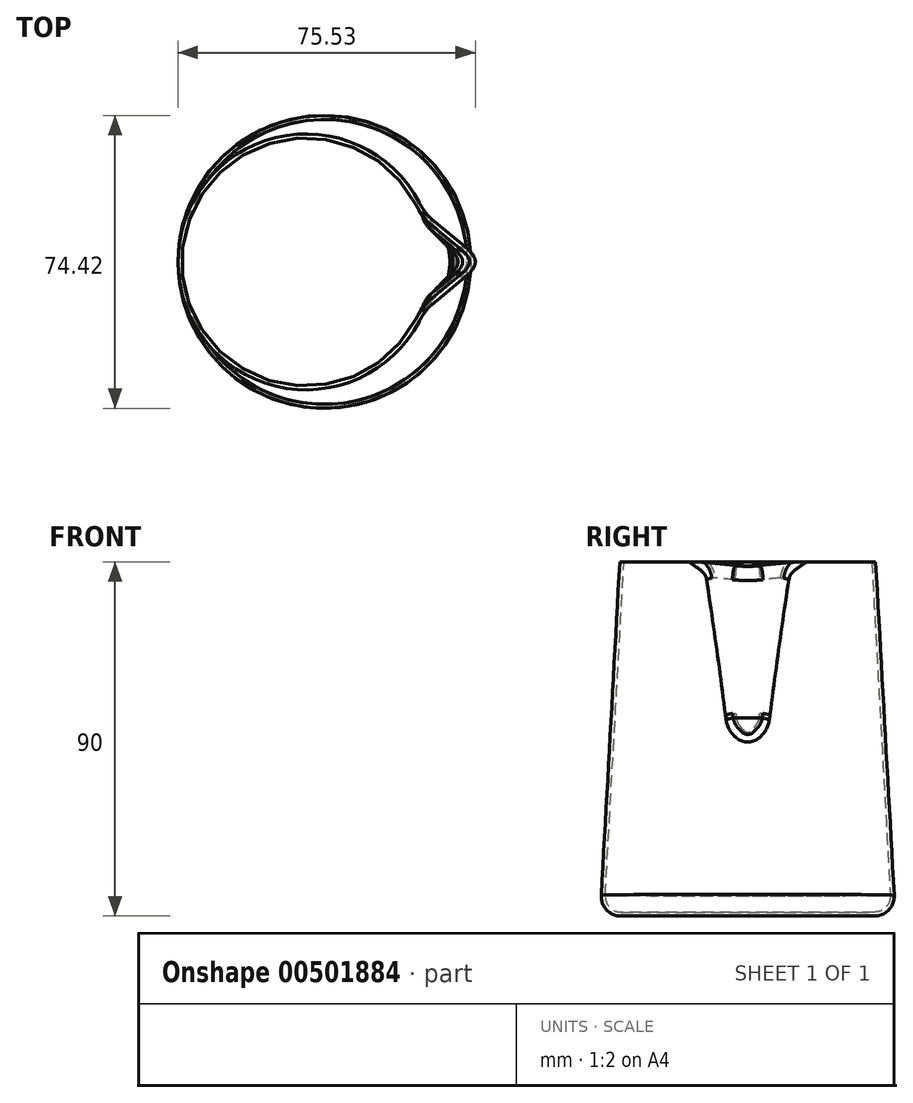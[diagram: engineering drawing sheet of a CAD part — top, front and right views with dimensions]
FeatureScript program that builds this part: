
annotation { "Feature Type Name" : "Feature", "Feature Type Description" : "" }
export const myFeature = defineFeature(function(context is Context, id is Id, definition is map)
    precondition{}
    {
        {
            var Q0;
            Q0=qCreatedBy(makeId("Top.planeOp"),FACE);
            var sketch = newSketch(context, id + "F0", { "sketchPlane" : qUnion([Q0])});
            skCircle(sketch, "E0", {"center": v(0, 0) * mm, "radius": 37.5 * mm});
            skSolve(sketch);
        }
        {
            var Q0;
            Q0=qCreatedBy(makeId("Top.planeOp"),FACE);
            cPlane(context, id + "F1", {"entities" : qUnion([Q0]), "cplaneType" : CPlaneType.OFFSET, "offset" : 90 * mm, "width" : 150 * mm, "height" : 150 * mm});
        }
        {
            var Q0;
            Q0=qCreatedBy(id+"F1.planeOp",FACE);
            var sketch = newSketch(context, id + "F2", { "sketchPlane" : qUnion([Q0])});
            skCircle(sketch, "E1", {"center": v(-5, 0) * mm, "radius": 32.5 * mm});
            skLineSegment(sketch, "E2", {"start": v(-111.32, 0) * mm, "end": v(0, 0) * mm, "construction": true});
            skSolve(sketch);
        }
        {
            var Q0;
            Q0=qCreatedBy(id+"F1.planeOp",FACE);
            var sketch = newSketch(context, id + "F3", { "sketchPlane" : qUnion([Q0])});
            skLineSegment(sketch, "E3", {"start": v(25, 44.02) * mm, "end": v(25, -44.23) * mm, "construction": true});
            skSolve(sketch);
        }
        {
            var Q0;
            Q0=qCreatedBy(id+"F1.planeOp",FACE);
            var Q1;
            Q1=sQuery(id+"F3.wireOp",EDGE,"E3");
            cPlane(context, id + "F4", {"entities" : qUnion([Q0, Q1]), "cplaneType" : CPlaneType.LINE_ANGLE, "offset" : 25 * mm, "angle" : 5 * degree, "oppositeDirection" : true, "width" : 150 * mm, "height" : 150 * mm});
        }
        {
            var Q0;
            Q0=qCreatedBy(id+"F4.planeOp",FACE);
            var sketch = newSketch(context, id + "F5", { "sketchPlane" : qUnion([Q0])});
            skLineSegment(sketch, "E4", {"start": v(17.06, -12.5) * mm, "end": v(32.06, 0) * mm});
            skLineSegment(sketch, "E5", {"start": v(0, 0) * mm, "end": v(86.07, 0) * mm, "construction": true});
            skPoint(sketch, "E6", {"position": v(43.04, 0) * mm});
            skLineSegment(sketch, "E7.MirrorCS", {"start": v(17.06, 12.5) * mm, "end": v(32.06, 0) * mm});
            skLineSegment(sketch, "E8", {"start": v(17.06, -12.5) * mm, "end": v(17.06, 12.5) * mm});
            skSolve(sketch);
        }
        {
            var Q0;
            Q0=makeQuery(id+"F0.imprint","IMPRINT",FACE,{"disambiguationData":[TD([[makeQuery(id+"F0.imprint","IMPRINT",EDGE,{"derivedFrom":sQuery(id+"F0.wireOp",EDGE,"E0")}),1.0]])]});
            var Q1;
            Q1=makeQuery(id+"F2.imprint","IMPRINT",FACE,{"disambiguationData":[TD([[makeQuery(id+"F2.imprint","IMPRINT",EDGE,{"derivedFrom":sQuery(id+"F2.wireOp",EDGE,"E1")}),1.0]])]});
            loft(context, id + "F6", {"sheetProfilesArray" : [{ "sheetProfileEntities" : qUnion([Q0]) }, { "sheetProfileEntities" : qUnion([Q1]) }]});
        }
        {
            var Q0;
            Q0=qCreatedBy(makeId("Front.planeOp"),FACE);
            var sketch = newSketch(context, id + "F7", { "sketchPlane" : qUnion([Q0])});
            skFitSpline(sketch, "E9", {"points": [v(-37.5, 90) * mm, v(-37.5, 0) * mm], "construction": true});
            skLineSegment(sketch, "E10", {"start": v(37.5, 0) * mm, "end": v(27.5, 90) * mm, "construction": true});
            skArc(sketch, "E11", {"start": v(38.1, 84.98) * mm, "mid": v(38.62, 87.04) * mm, "end": v(39.94, 88.7) * mm});
            skLineSegment(sketch, "E12", {"start": v(36.93, 49.98) * mm, "end": v(38.1, 84.98) * mm});
            skArc(sketch, "E13", {"start": v(32.48, 45.18) * mm, "mid": v(35.6, 46.75) * mm, "end": v(36.93, 49.98) * mm});
            skSolve(sketch);
        }
        {
            var Q0;
            Q0=makeQuery(id+"F5.imprint","IMPRINT",FACE,{"disambiguationData":[TD([[makeQuery(id+"F5.imprint","IMPRINT",EDGE,{"derivedFrom":sQuery(id+"F5.wireOp",EDGE,"E4")}),1.0]])]});
            var Q1;
            Q1=sQuery(id+"F7.wireOp",EDGE,"E12");
            var Q2;
            Q2=sQuery(id+"F7.wireOp",EDGE,"E13");
            var Q3;
            Q3=sQuery(id+"F7.wireOp",EDGE,"E11");
            sweep(context, id + "F8", {"operationType" : NewBodyOperationType.ADD, "profiles" : qUnion([Q0]), "path" : qUnion([Q1, Q2, Q3]), "keepProfileOrientation" : true});
        }
        {
            var Q0;
            Q0=qCreatedBy(id+"F4.planeOp",FACE);
            var sketch = newSketch(context, id + "F9", { "sketchPlane" : qUnion([Q0])});
            skLineSegment(sketch, "E14", {"start": v(17.06, -12.5) * mm, "end": v(32.06, 0) * mm});
            skLineSegment(sketch, "E15", {"start": v(32.06, 0) * mm, "end": v(17.06, 12.5) * mm});
            skLineSegment(sketch, "E16", {"start": v(17.06, 12.5) * mm, "end": v(17.06, -12.5) * mm});
            skSolve(sketch);
        }
        {
            var Q0;
            Q0 = qSketchRegion(id + "F9", true);
            extrude(context, id + "F10", {"entities" : qUnion([Q0]), "operationType" : NewBodyOperationType.REMOVE, "oppositeDirection" : true, "depth" : 25 * mm});
        }
        {
            var Q0;
            Q0=makeQuery(id+"F8.opSweep","SWEPT_EDGE",EDGE,{"disambiguationData":[OSD([sQuery(id+"F5.wireOp",EDGE,"E4"),sQuery(id+"F5.wireOp",EDGE,"E7.MirrorCS"),sQuery(id+"F7.wireOp",EDGE,"E12")])]});
            fillet(context, id + "F11", {"entities" : qUnion([Q0]), "radius" : 5 * mm, "tangentPropagation" : true, "rho" : 0.5, "crossSection" : FilletCrossSection.CONIC, "allowEdgeOverflow" : false});
        }
        {
            var Q0;
            Q0=makeQuery(id+"F8.boolean.opBoolean","INTERSECT",EDGE,{"derivedFrom":[makeQuery(id+"F6.opLoft","SWEPT_FACE",FACE,{"disambiguationData":[OSD([sQuery(id+"F0.wireOp",EDGE,"E0"),sQuery(id+"F2.wireOp",EDGE,"E1")])]}),makeQuery(id+"F8.opSweep","SWEPT_FACE",FACE,{"disambiguationData":[OSD([sQuery(id+"F5.wireOp",EDGE,"E7.MirrorCS"),sQuery(id+"F7.wireOp",EDGE,"E12")])]})]});
            var Q1;
            Q1=makeQuery(id+"F8.boolean.opBoolean","INTERSECT",EDGE,{"derivedFrom":[makeQuery(id+"F6.opLoft","SWEPT_FACE",FACE,{"disambiguationData":[OSD([sQuery(id+"F0.wireOp",EDGE,"E0"),sQuery(id+"F2.wireOp",EDGE,"E1")])]}),makeQuery(id+"F8.opSweep","SWEPT_FACE",FACE,{"disambiguationData":[OSD([sQuery(id+"F5.wireOp",EDGE,"E7.MirrorCS"),sQuery(id+"F7.wireOp",EDGE,"E11")])]})]});
            var Q2;
            Q2=makeQuery(id+"F8.boolean.opBoolean","INTERSECT",EDGE,{"derivedFrom":[makeQuery(id+"F6.opLoft","SWEPT_FACE",FACE,{"disambiguationData":[OSD([sQuery(id+"F0.wireOp",EDGE,"E0"),sQuery(id+"F2.wireOp",EDGE,"E1")])]}),makeQuery(id+"F8.opSweep","SWEPT_FACE",FACE,{"disambiguationData":[OSD([sQuery(id+"F5.wireOp",EDGE,"E7.MirrorCS"),sQuery(id+"F7.wireOp",EDGE,"E13")])]})]});
            var Q3;
            {var subQ0=sQuery(id+"F5.wireOp",EDGE,"E7.MirrorCS");var subQ1=sQuery(id+"F5.wireOp",EDGE,"E4");var subQ2=sQuery(id+"F2.wireOp",EDGE,"E1");var subQ3=sQuery(id+"F7.wireOp",EDGE,"E11");var subQ4=sQuery(id+"F0.wireOp",EDGE,"E0");var subQ5=sQuery(id+"F7.wireOp",EDGE,"E13");var subQ6=makeQuery(id+"F6.opLoft","SWEPT_FACE",FACE,{"disambiguationData":[OSD([subQ4,subQ2])]});var subQ7=sQuery(id+"F7.wireOp",EDGE,"E12");Q3=makeQuery(id+"F11.opFillet","BLEND_EDGE",EDGE,{"blendedFrom":[makeQuery(id+"F8.opSweep","SWEPT_EDGE",EDGE,{"disambiguationData":[OSD([subQ1,subQ0,subQ5])]}),makeQuery(id+"F8.boolean.opBoolean","SPLIT",FACE,{"disambiguationData":[TD([subQ6,makeQuery(id+"F6.opLoft","CAP_FACE",FACE,{"disambiguationData":[OSD([makeQuery(id+"F0.imprint","IMPRINT",FACE,{"disambiguationData":[TD([[makeQuery(id+"F0.imprint","IMPRINT",EDGE,{"derivedFrom":subQ4}),1.0]])]})])],"isStart":true}),makeQuery(id+"F6.opLoft","CAP_FACE",FACE,{"disambiguationData":[OSD([makeQuery(id+"F2.imprint","IMPRINT",FACE,{"disambiguationData":[TD([[makeQuery(id+"F2.imprint","IMPRINT",EDGE,{"derivedFrom":subQ2}),1.0]])]})])],"isStart":true}),makeQuery(id+"F8.opSweep","CAP_FACE",FACE,{"disambiguationData":[OSD([subQ1,subQ0,sQuery(id+"F5.wireOp",EDGE,"E8"),sQuery(id+"F7.wireOp",VERTEX,"E11.end")])],"isStart":true}),makeQuery(id+"F8.opSweep","SWEPT_FACE",FACE,{"disambiguationData":[OSD([subQ1,subQ3])]}),makeQuery(id+"F8.opSweep","SWEPT_FACE",FACE,{"disambiguationData":[OSD([subQ1,subQ7])]}),makeQuery(id+"F8.opSweep","SWEPT_FACE",FACE,{"disambiguationData":[OSD([subQ1,subQ5])]}),makeQuery(id+"F8.opSweep","SWEPT_FACE",FACE,{"disambiguationData":[OSD([subQ0,subQ3])]}),makeQuery(id+"F8.opSweep","SWEPT_FACE",FACE,{"disambiguationData":[OSD([subQ0,subQ7])]}),makeQuery(id+"F8.opSweep","SWEPT_FACE",FACE,{"disambiguationData":[OSD([subQ0,subQ5])]})])],"derivedFrom":subQ6})],"blendedInto":[makeQuery(id+"F8.boolean.opBoolean","SPLIT",FACE,{"disambiguationData":[TD([subQ6,makeQuery(id+"F6.opLoft","CAP_FACE",FACE,{"disambiguationData":[OSD([makeQuery(id+"F0.imprint","IMPRINT",FACE,{"disambiguationData":[TD([[makeQuery(id+"F0.imprint","IMPRINT",EDGE,{"derivedFrom":subQ4}),1.0]])]})])],"isStart":true}),makeQuery(id+"F6.opLoft","CAP_FACE",FACE,{"disambiguationData":[OSD([makeQuery(id+"F2.imprint","IMPRINT",FACE,{"disambiguationData":[TD([[makeQuery(id+"F2.imprint","IMPRINT",EDGE,{"derivedFrom":subQ2}),1.0]])]})])],"isStart":true}),makeQuery(id+"F8.opSweep","CAP_FACE",FACE,{"disambiguationData":[OSD([subQ1,subQ0,sQuery(id+"F5.wireOp",EDGE,"E8"),sQuery(id+"F7.wireOp",VERTEX,"E11.end")])],"isStart":true}),makeQuery(id+"F8.opSweep","SWEPT_FACE",FACE,{"disambiguationData":[OSD([subQ1,subQ3])]}),makeQuery(id+"F8.opSweep","SWEPT_FACE",FACE,{"disambiguationData":[OSD([subQ1,subQ7])]}),makeQuery(id+"F8.opSweep","SWEPT_FACE",FACE,{"disambiguationData":[OSD([subQ1,subQ5])]}),makeQuery(id+"F8.opSweep","SWEPT_FACE",FACE,{"disambiguationData":[OSD([subQ0,subQ3])]}),makeQuery(id+"F8.opSweep","SWEPT_FACE",FACE,{"disambiguationData":[OSD([subQ0,subQ7])]}),makeQuery(id+"F8.opSweep","SWEPT_FACE",FACE,{"disambiguationData":[OSD([subQ0,subQ5])]})])],"derivedFrom":subQ6})]});}
            var Q4;
            Q4=makeQuery(id+"F8.boolean.opBoolean","INTERSECT",EDGE,{"derivedFrom":[makeQuery(id+"F6.opLoft","SWEPT_FACE",FACE,{"disambiguationData":[OSD([sQuery(id+"F0.wireOp",EDGE,"E0"),sQuery(id+"F2.wireOp",EDGE,"E1")])]}),makeQuery(id+"F8.opSweep","SWEPT_FACE",FACE,{"disambiguationData":[OSD([sQuery(id+"F5.wireOp",EDGE,"E4"),sQuery(id+"F7.wireOp",EDGE,"E13")])]})]});
            var Q5;
            Q5=makeQuery(id+"F8.boolean.opBoolean","INTERSECT",EDGE,{"derivedFrom":[makeQuery(id+"F6.opLoft","SWEPT_FACE",FACE,{"disambiguationData":[OSD([sQuery(id+"F0.wireOp",EDGE,"E0"),sQuery(id+"F2.wireOp",EDGE,"E1")])]}),makeQuery(id+"F8.opSweep","SWEPT_FACE",FACE,{"disambiguationData":[OSD([sQuery(id+"F5.wireOp",EDGE,"E4"),sQuery(id+"F7.wireOp",EDGE,"E12")])]})]});
            fillet(context, id + "F12", {"entities" : qUnion([Q0, Q1, Q2, Q3, Q4, Q5]), "radius" : 3 * mm, "tangentPropagation" : true, "allowEdgeOverflow" : false});
        }
        {
            var Q0;
            Q0=makeQuery(id+"F6.opLoft","MID_CAP_EDGE",EDGE,{"disambiguationData":[OSD([sQuery(id+"F0.wireOp",EDGE,"E0")])],"capPos":0.0});
            fillet(context, id + "F13", {"entities" : qUnion([Q0]), "radius" : 5 * mm, "tangentPropagation" : true, "allowEdgeOverflow" : false});
        }
        {
            var Q0;
            Q0=makeQuery(id+"F6.opLoft","CAP_FACE",FACE,{"disambiguationData":[OSD([makeQuery(id+"F2.imprint","IMPRINT",FACE,{"disambiguationData":[TD([[makeQuery(id+"F2.imprint","IMPRINT",EDGE,{"derivedFrom":sQuery(id+"F2.wireOp",EDGE,"E1")}),1.0]])]})])],"isStart":true});
            var Q1;
            Q1=makeQuery(id+"F10.boolean.opBoolean","MERGE",FACE,{"derivedFrom":[makeQuery(id+"F8.opSweep","CAP_FACE",FACE,{"disambiguationData":[OSD([sQuery(id+"F5.wireOp",EDGE,"E4"),sQuery(id+"F5.wireOp",EDGE,"E7.MirrorCS"),sQuery(id+"F5.wireOp",EDGE,"E8"),sQuery(id+"F7.wireOp",VERTEX,"E11.end")])],"isStart":true}),makeQuery(id+"F10.opExtrude","CAP_FACE",FACE,{"disambiguationData":[OSD([sQuery(id+"F9.wireOp",EDGE,"E14"),sQuery(id+"F9.wireOp",EDGE,"E15"),sQuery(id+"F9.wireOp",EDGE,"E16")])],"isStart":true})]});
            shell(context, id + "F14", {"entities" : qUnion([Q0, Q1]), "thickness" : 1 * mm});
        }
        {
            var Q0;
            Q0=qCreatedBy(makeId("Right.planeOp"),FACE);
            cPlane(context, id + "F15", {"entities" : qUnion([Q0]), "cplaneType" : CPlaneType.OFFSET, "offset" : 37.5 * mm, "oppositeDirection" : true, "width" : 150 * mm, "height" : 150 * mm});
        }
    });
